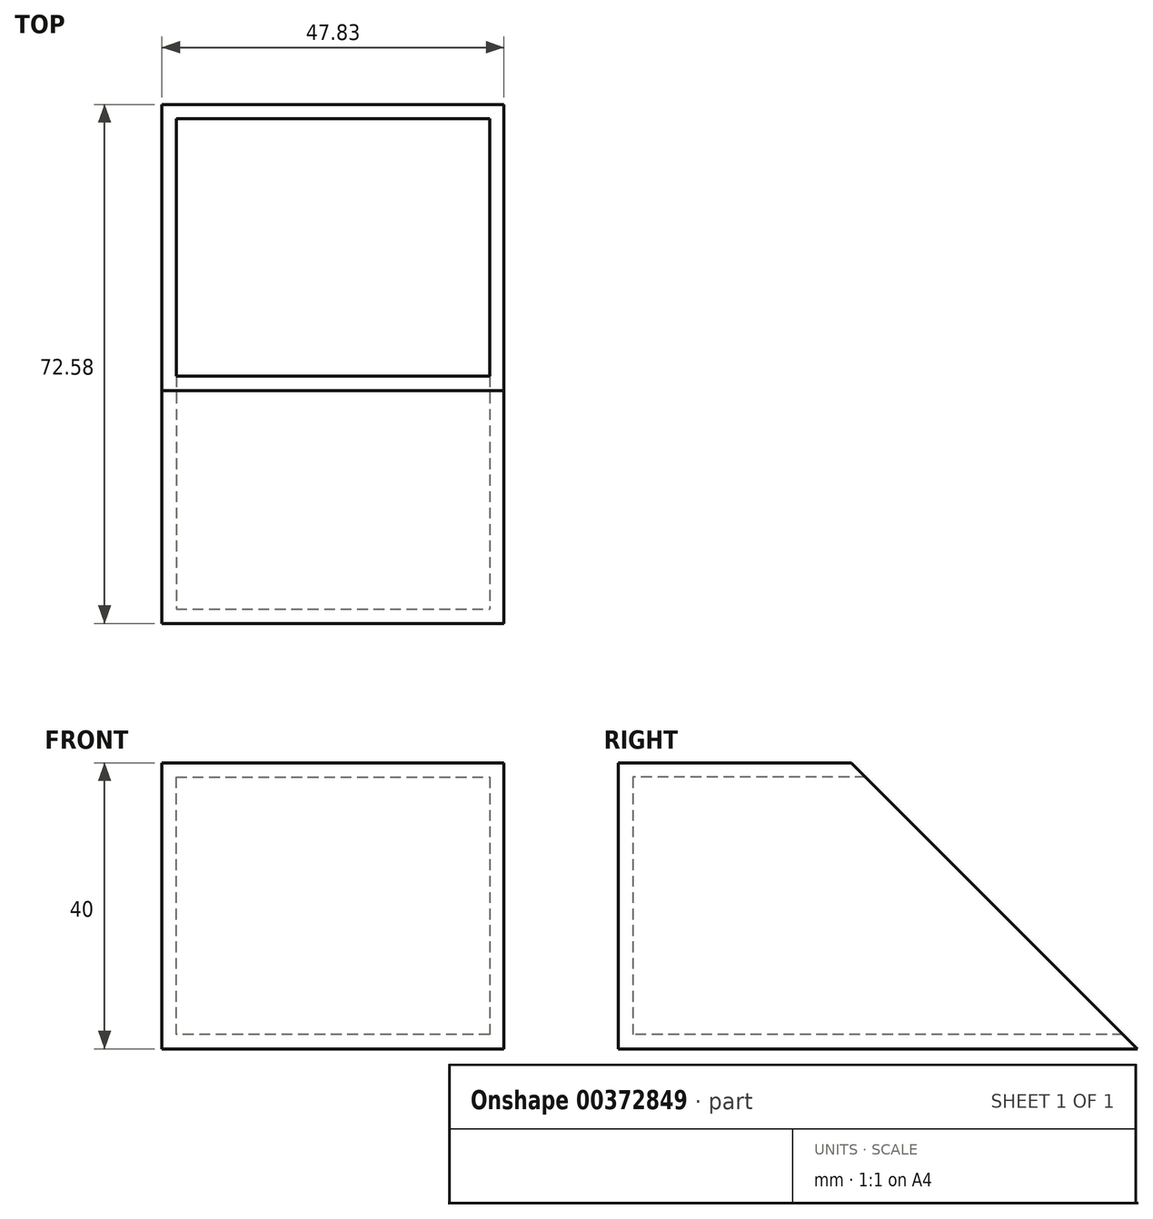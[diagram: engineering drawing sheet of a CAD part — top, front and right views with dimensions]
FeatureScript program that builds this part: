
annotation { "Feature Type Name" : "Feature", "Feature Type Description" : "" }
export const myFeature = defineFeature(function(context is Context, id is Id, definition is map)
    precondition{}
    {
        {
            var Q0;
            Q0=qCreatedBy(makeId("Top.planeOp"),FACE);
            var sketch = newSketch(context, id + "F0", { "sketchPlane" : qUnion([Q0])});
            skLineSegment(sketch, "E0.bottom", {"start": v(-64.5, 27.54) * mm, "end": v(-16.67, 27.54) * mm});
            skLineSegment(sketch, "E0.top", {"start": v(-64.5, -49.04) * mm, "end": v(-16.67, -49.04) * mm});
            skLineSegment(sketch, "E0.left", {"start": v(-64.5, 27.54) * mm, "end": v(-64.5, -49.04) * mm});
            skLineSegment(sketch, "E0.right", {"start": v(-16.67, 27.54) * mm, "end": v(-16.67, -49.04) * mm});
            skSolve(sketch);
        }
        {
            var Q0;
            Q0=makeQuery(id+"F0.imprint","IMPRINT",FACE,{"disambiguationData":[TD([[makeQuery(id+"F0.imprint","IMPRINT",EDGE,{"derivedFrom":sQuery(id+"F0.wireOp",EDGE,"E0.bottom")}),-1.0]])]});
            extrude(context, id + "F1", {"entities" : qUnion([Q0]), "depth" : 40 * mm});
        }
        {
            var Q0;
            Q0=makeQuery(id+"F1.opExtrude","CAP_EDGE",EDGE,{"disambiguationData":[OSD([sQuery(id+"F0.wireOp",EDGE,"E0.bottom")])],"isStart":false});
            chamfer(context, id + "F2", {"entities" : qUnion([Q0]), "width" : 44 * mm, "tangentPropagation" : true});
        }
        {
            var Q0;
            Q0=makeQuery(id+"F2.opChamfer","BLEND_FACE",FACE,{"disambiguationData":[OSD([sQuery(id+"F0.wireOp",EDGE,"E0.bottom")])]});
            shell(context, id + "F3", {"entities" : qUnion([Q0]), "thickness" : 2 * mm});
        }
    });
